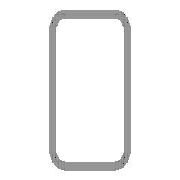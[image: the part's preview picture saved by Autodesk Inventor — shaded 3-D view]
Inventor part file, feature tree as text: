
AUTODESK INVENTOR PART (.ipt)
format: ipt  version: 2025.1 (Build 291241020, 241B)  size: 133,632 bytes
history: native  units: mm (DEFAULTED — no unit token found)
features: other x4, sketch x1, plane x1
ambient origin geometry x8: Origin, YZ Plane, XZ Plane, XY Plane, X Axis, Y Axis, Z Axis, Center Point
bodies: Solid1 (feature_tree), Body (feature_tree)
feature tree (6):
  parser-record x1  (decoder bookkeeping rows leaked as tree rows — omitted from the tree; the rows remain in map.json)
  other  "Driven Length"
  other  "Start Plane"
  other  "End Plane"
  sketch  "Sketch3"  dims[d3=1220.0mm d4=0.0mm d7=4.0mm d9=20.0mm d11=40.0mm d12=2.0mm d13=-0.0mm d14=1220.0mm d15=10.0mm d16=20.0mm d17=90.0deg d18=1220.0mm]
  plane  "Work Plane3"
